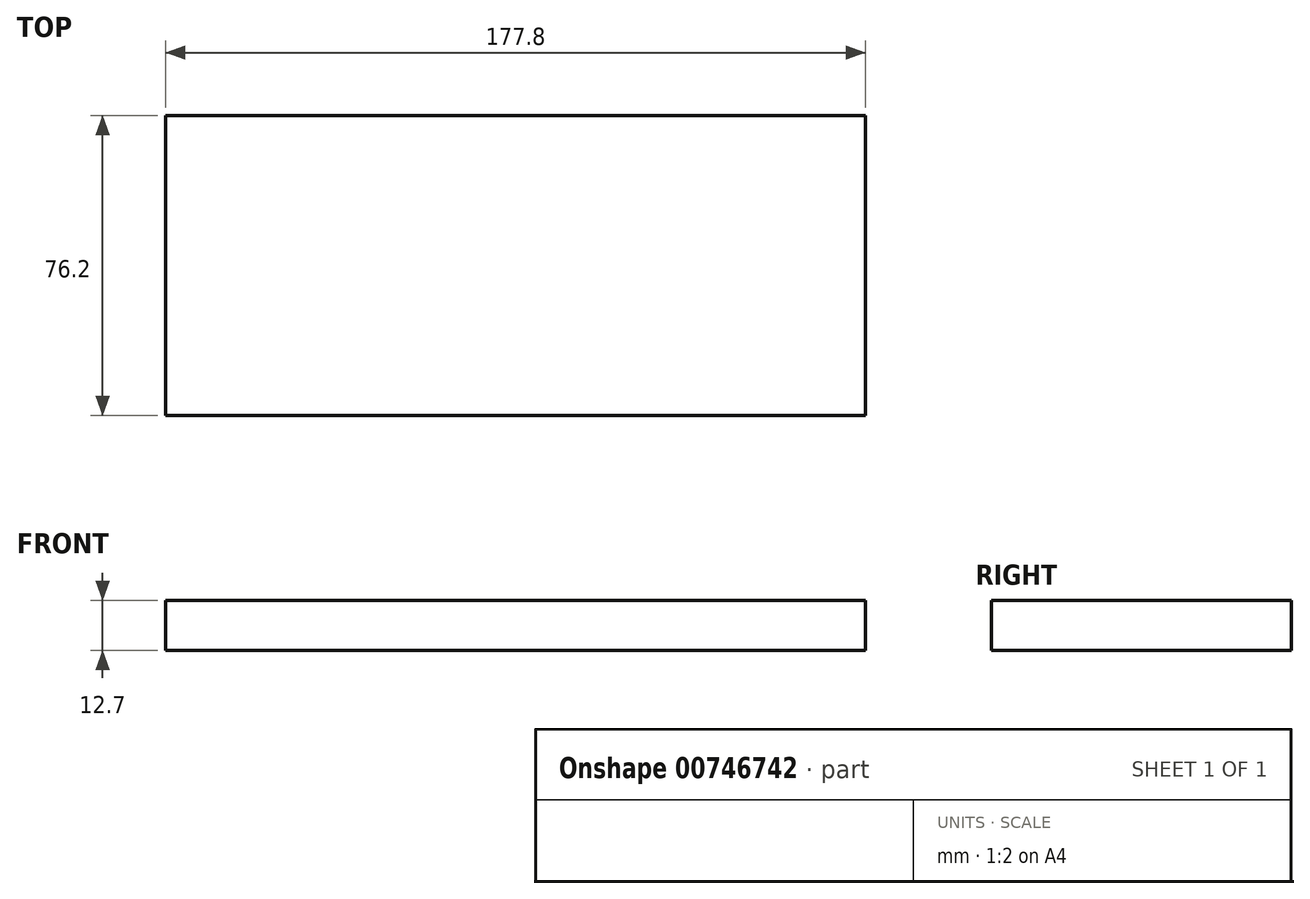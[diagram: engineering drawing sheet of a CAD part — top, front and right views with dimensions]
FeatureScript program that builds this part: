
annotation { "Feature Type Name" : "Feature", "Feature Type Description" : "" }
export const myFeature = defineFeature(function(context is Context, id is Id, definition is map)
    precondition{}
    {
        {
            var Q0;
            Q0=qCreatedBy(makeId("Front.planeOp"),FACE);
            var sketch = newSketch(context, id + "F0", { "sketchPlane" : qUnion([Q0])});
            skLineSegment(sketch, "E0.bottom", {"start": v(-89.05, 12.7) * mm, "end": v(88.75, 12.7) * mm});
            skLineSegment(sketch, "E0.top", {"start": v(-89.05, 0) * mm, "end": v(88.75, 0) * mm});
            skLineSegment(sketch, "E0.left", {"start": v(-89.05, 12.7) * mm, "end": v(-89.05, 0) * mm});
            skLineSegment(sketch, "E0.right", {"start": v(88.75, 12.7) * mm, "end": v(88.75, 0) * mm});
            skSolve(sketch);
        }
        {
            var Q0;
            Q0=makeQuery(id+"F0.imprint","IMPRINT",FACE,{"disambiguationData":[TD([[makeQuery(id+"F0.imprint","IMPRINT",EDGE,{"derivedFrom":sQuery(id+"F0.wireOp",EDGE,"E0.bottom")}),-1.0]])]});
            extrude(context, id + "F1", {"entities" : qUnion([Q0]), "depth" : 76.2 * mm, "offsetDistance" : 25.4 * mm});
        }
    });
